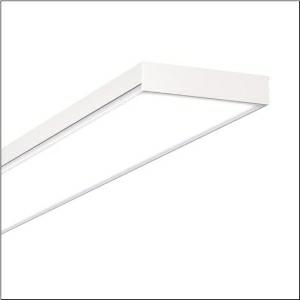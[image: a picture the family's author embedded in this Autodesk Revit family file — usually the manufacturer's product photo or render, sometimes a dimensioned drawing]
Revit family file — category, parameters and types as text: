
# Revit family: apollon_r__31_51mp25wd2441w_8f76
name_source: partatom
category: Lighting Fixtures
units: mm (PartAtom-declared; Revit-internal decimal feet)

## family parameters
Cut with Voids When Loaded = No
Host = Face
Light Source = No
Part Type = Normal
Room Calculation Point = No
Round Connector Dimension = Use Diameter
Shared = No

## types (1)
- Apollon® 31 (1 x LED, 3800 lm, 28 W, 4000K)
    Apparent Load = 28 VA
    CIE Flux Codes = 61 87 97 97 100
    Color Rendering = 80
    Color Temperature = 4000K
    Default Elevation = 1800 mm
    Description = Apollon® 31, office luminaire, primary optical cover: micro prismatic cover, of PMMA, light emission: direct distribution, primary light characteristic: symmetric, installation type: surface-mounted, LED, rated luminous flux: 3.800lm, luminous efficacy: 134lm/W, light colour: 840, colour temperature: 4000K, control gear: ECG DALI, with terminal, 5-pole, mains connection: 220..240V, AC, 50/60Hz, rated input power: 28W, housing, of sheet steel, coil coated, traffic white (RAL 9016), length: 1.245mm, width: 200mm, height: 44mm, protection rating (complete): IP20, insulation class (complete): insulation class II (safety insulation), certification: CE, impact resistance: IK02, permissible operating ambient temperature: -20..+40°C, standard: EN 60598-2-22, packaging unit: 1 piece
    Height = 44 mm
    Lamp = 1 x LED
    Lamp Light Flux = 3800 lm
    Lamp Power = 28 W
    Lamp count = 1
    Length = 1245 mm
    Luminous efficacy = 136 lm/W
    Manufacturer = Siteco
    ModVariant = No
    Model = 51MP25WD2441W
    Mounting Place = Ceiling
    Mounting Type = Surface mounted
    Number of Poles = 1
    OnlyDefault = Yes
    Power Factor = 1
    Product Name = Apollon® 31
    Product group = office luminaire | ceiling mounted
    ProductGroupID = 302
    Protection Class = Protection class II
    Protection Degree = IP 20
    RLX_Detail_Level = 1
    RlxData = <blob elided: 20733 chars, md5=5485af97>
    Socket = socket
    Standby Power = 0 W
    System Light Flux = 3800 lm
    System Power = 28 W
    Type Comments = Product without accessories
    Type Image = l_1007095.jpg
    URL = http://relux.com
    VarID = ---
    Voltage = 0 V
    Weight = 0.00 kg
    Width = 200 mm  [stored 0.656168 ft]

note: [stored X ft] marks values corroborated as IEEE doubles in the binary element streams (Revit-internal decimal feet)

## geometry (parser evidence)
native form markers: Blend x4, Sweep x10
no freeform markers — native parametric forms only
